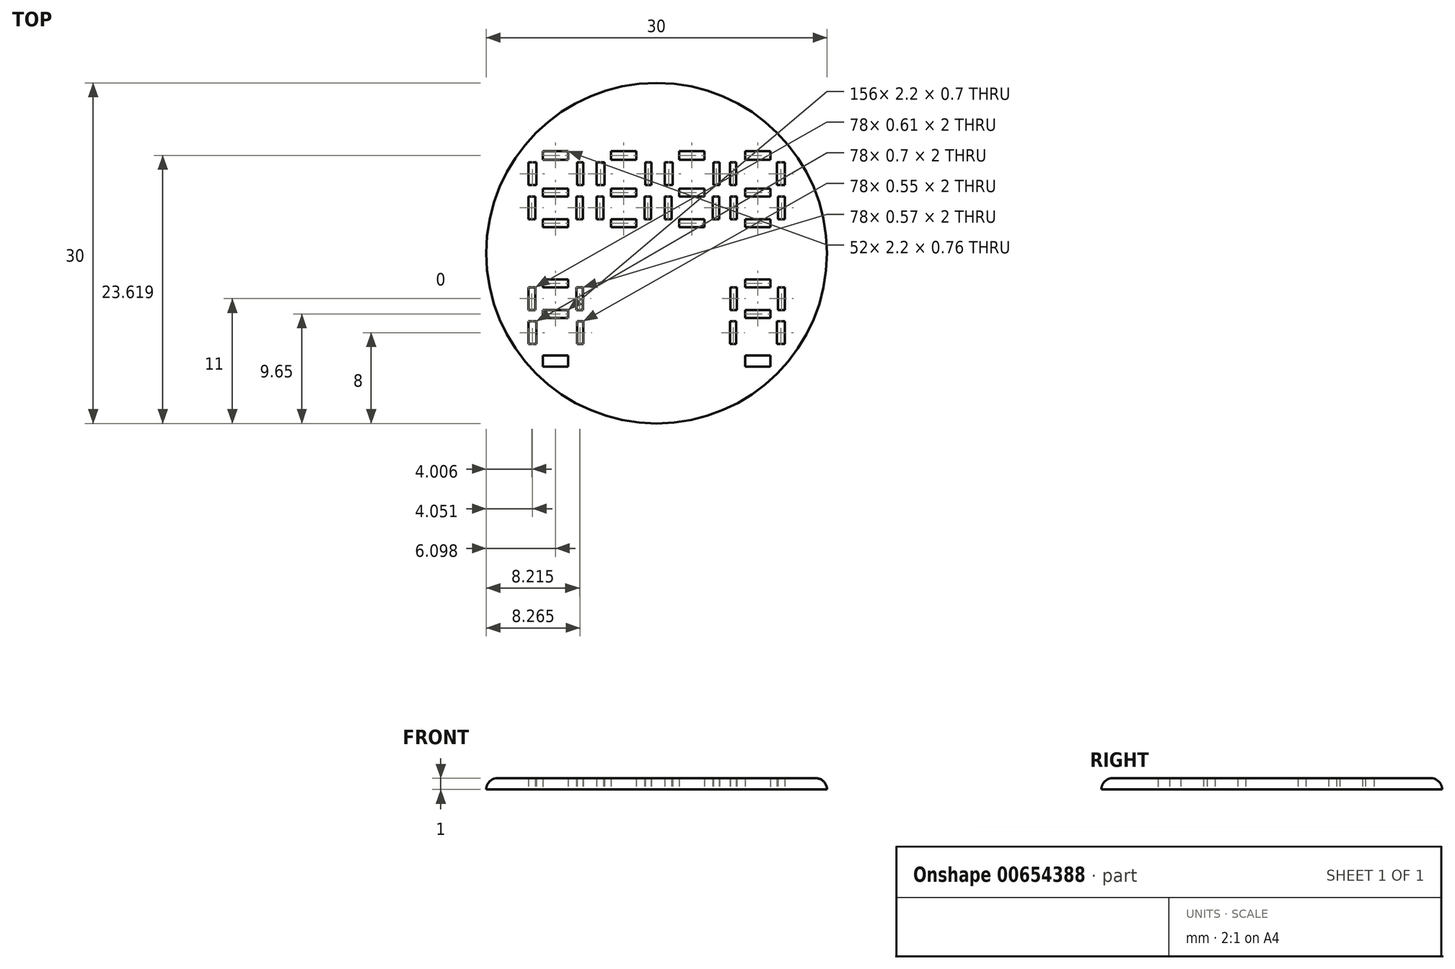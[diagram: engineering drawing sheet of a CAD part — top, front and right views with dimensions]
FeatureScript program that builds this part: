
annotation { "Feature Type Name" : "Feature", "Feature Type Description" : "" }
export const myFeature = defineFeature(function(context is Context, id is Id, definition is map)
    precondition{}
    {
        {
            var Q0;
            Q0=qCreatedBy(makeId("Top.planeOp"),FACE);
            var sketch = newSketch(context, id + "F0", { "sketchPlane" : qUnion([Q0])});
            skCircle(sketch, "E0", {"center": v(0, 0) * mm, "radius": 15 * mm});
            skLineSegment(sketch, "E1.bottom", {"start": v(-6.46, -6) * mm, "end": v(-7, -6) * mm});
            skLineSegment(sketch, "E1.top", {"start": v(-6.46, -8) * mm, "end": v(-7, -8) * mm});
            skLineSegment(sketch, "E1.left", {"start": v(-6.46, -6) * mm, "end": v(-6.46, -8) * mm});
            skLineSegment(sketch, "E1.right", {"start": v(-7, -6) * mm, "end": v(-7, -8) * mm});
            skLineSegment(sketch, "E2.bottom", {"start": v(-7.07, -5) * mm, "end": v(-6.5, -5) * mm});
            skLineSegment(sketch, "E2.top", {"start": v(-7.07, -3) * mm, "end": v(-6.5, -3) * mm});
            skLineSegment(sketch, "E2.left", {"start": v(-7.07, -5) * mm, "end": v(-7.07, -3) * mm});
            skLineSegment(sketch, "E2.right", {"start": v(-6.5, -5) * mm, "end": v(-6.5, -3) * mm});
            skLineSegment(sketch, "E3.bottom", {"start": v(-7.8, -5) * mm, "end": v(-10, -5) * mm});
            skLineSegment(sketch, "E3.top", {"start": v(-7.8, -5.7) * mm, "end": v(-10, -5.7) * mm});
            skLineSegment(sketch, "E3.left", {"start": v(-7.8, -5) * mm, "end": v(-7.8, -5.7) * mm});
            skLineSegment(sketch, "E3.right", {"start": v(-10, -5) * mm, "end": v(-10, -5.7) * mm});
            skLineSegment(sketch, "E4.bottom", {"start": v(-7.8, -9) * mm, "end": v(-10, -9) * mm});
            skLineSegment(sketch, "E4.top", {"start": v(-7.8, -9) * mm, "end": v(-10, -9) * mm});
            skLineSegment(sketch, "E4.left", {"start": v(-7.8, -9) * mm, "end": v(-7.8, -9) * mm});
            skLineSegment(sketch, "E4.right", {"start": v(-10, -9) * mm, "end": v(-10, -9) * mm});
            skLineSegment(sketch, "E5.bottom", {"start": v(-10, -3) * mm, "end": v(-7.8, -3) * mm});
            skLineSegment(sketch, "E5.top", {"start": v(-10, -2.3) * mm, "end": v(-7.8, -2.3) * mm});
            skLineSegment(sketch, "E5.left", {"start": v(-10, -3) * mm, "end": v(-10, -2.3) * mm});
            skLineSegment(sketch, "E5.right", {"start": v(-7.8, -3) * mm, "end": v(-7.8, -2.3) * mm});
            skPoint(sketch, "E6.firstSnap0", {"position": v(-8.9, -3) * mm});
            skLineSegment(sketch, "E6.bottom", {"start": v(-10.69, -3) * mm, "end": v(-11.3, -3) * mm});
            skLineSegment(sketch, "E6.top", {"start": v(-10.69, -5) * mm, "end": v(-11.3, -5) * mm});
            skLineSegment(sketch, "E6.left", {"start": v(-10.69, -3) * mm, "end": v(-10.69, -5) * mm});
            skLineSegment(sketch, "E6.right", {"start": v(-11.3, -3) * mm, "end": v(-11.3, -5) * mm});
            skLineSegment(sketch, "E7.bottom", {"start": v(-10.6, -6) * mm, "end": v(-11.3, -6) * mm});
            skLineSegment(sketch, "E7.top", {"start": v(-10.6, -8) * mm, "end": v(-11.3, -8) * mm});
            skLineSegment(sketch, "E7.left", {"start": v(-10.6, -6) * mm, "end": v(-10.6, -8) * mm});
            skLineSegment(sketch, "E7.right", {"start": v(-11.3, -6) * mm, "end": v(-11.3, -8) * mm});
            skLineSegment(sketch, "E8.MirrorCS", {"start": v(10.69, -3) * mm, "end": v(10.69, -5) * mm});
            skLineSegment(sketch, "E9.MirrorCS", {"start": v(10.69, -5) * mm, "end": v(11.3, -5) * mm});
            skLineSegment(sketch, "E10.MirrorCS", {"start": v(11.3, -3) * mm, "end": v(11.3, -5) * mm});
            skLineSegment(sketch, "E11.MirrorCS", {"start": v(10.69, -3) * mm, "end": v(11.3, -3) * mm});
            skLineSegment(sketch, "E12.MirrorCS", {"start": v(7.8, -5.7) * mm, "end": v(10, -5.7) * mm});
            skLineSegment(sketch, "E13.MirrorCS", {"start": v(7.8, -5) * mm, "end": v(10, -5) * mm});
            skLineSegment(sketch, "E14.MirrorCS", {"start": v(7.8, -5) * mm, "end": v(7.8, -5.7) * mm});
            skLineSegment(sketch, "E15.MirrorCS", {"start": v(7.07, -5) * mm, "end": v(6.5, -5) * mm});
            skLineSegment(sketch, "E16.MirrorCS", {"start": v(6.5, -5) * mm, "end": v(6.5, -3) * mm});
            skLineSegment(sketch, "E17.MirrorCS", {"start": v(7.07, -3) * mm, "end": v(6.5, -3) * mm});
            skLineSegment(sketch, "E18.MirrorCS", {"start": v(7.07, -5) * mm, "end": v(7.07, -3) * mm});
            skLineSegment(sketch, "E19.MirrorCS", {"start": v(6.46, -6) * mm, "end": v(7, -6) * mm});
            skLineSegment(sketch, "E20.MirrorCS", {"start": v(6.46, -6) * mm, "end": v(6.46, -8) * mm});
            skLineSegment(sketch, "E21.MirrorCS", {"start": v(6.46, -8) * mm, "end": v(7, -8) * mm});
            skLineSegment(sketch, "E22.MirrorCS", {"start": v(7, -6) * mm, "end": v(7, -8) * mm});
            skLineSegment(sketch, "E23.MirrorCS", {"start": v(7.8, -9) * mm, "end": v(10, -9) * mm});
            skLineSegment(sketch, "E24.MirrorCS", {"start": v(7.8, -9) * mm, "end": v(7.8, -9) * mm});
            skLineSegment(sketch, "E25.MirrorCS", {"start": v(10, -9) * mm, "end": v(10, -9) * mm});
            skLineSegment(sketch, "E26.MirrorCS", {"start": v(10.6, -6) * mm, "end": v(10.6, -8) * mm});
            skLineSegment(sketch, "E27.MirrorCS", {"start": v(11.3, -6) * mm, "end": v(11.3, -8) * mm});
            skLineSegment(sketch, "E28.MirrorCS", {"start": v(10.6, -8) * mm, "end": v(11.3, -8) * mm});
            skLineSegment(sketch, "E29.MirrorCS", {"start": v(10.6, -6) * mm, "end": v(11.3, -6) * mm});
            skLineSegment(sketch, "E30.MirrorCS", {"start": v(10, -3) * mm, "end": v(7.8, -3) * mm});
            skLineSegment(sketch, "E31.MirrorCS", {"start": v(10, -2.3) * mm, "end": v(7.8, -2.3) * mm});
            skLineSegment(sketch, "E32.MirrorCS", {"start": v(10, -3) * mm, "end": v(10, -2.3) * mm});
            skLineSegment(sketch, "E33.MirrorCS", {"start": v(7.8, -3) * mm, "end": v(7.8, -2.3) * mm});
            skLineSegment(sketch, "E34", {"start": v(10, -5) * mm, "end": v(10, -5.7) * mm});
            skLineSegment(sketch, "E35.MirrorCS", {"start": v(-7.8, 5) * mm, "end": v(-10, 5) * mm});
            skLineSegment(sketch, "E36.MirrorCS", {"start": v(-7.8, 5.7) * mm, "end": v(-10, 5.7) * mm});
            skLineSegment(sketch, "E37.MirrorCS", {"start": v(-7.8, 5) * mm, "end": v(-7.8, 5.7) * mm});
            skLineSegment(sketch, "E38.MirrorCS", {"start": v(-10, 5) * mm, "end": v(-10, 5.7) * mm});
            skLineSegment(sketch, "E39.MirrorCS", {"start": v(-7, 6) * mm, "end": v(-7, 8) * mm});
            skLineSegment(sketch, "E40.MirrorCS", {"start": v(-6.46, 6) * mm, "end": v(-7, 6) * mm});
            skLineSegment(sketch, "E41.MirrorCS", {"start": v(-6.46, 6) * mm, "end": v(-6.46, 8) * mm});
            skLineSegment(sketch, "E42.MirrorCS", {"start": v(-6.46, 8) * mm, "end": v(-7, 8) * mm});
            skLineSegment(sketch, "E43.MirrorCS", {"start": v(-6.5, 5) * mm, "end": v(-6.5, 3) * mm});
            skLineSegment(sketch, "E44.MirrorCS", {"start": v(-7.07, 5) * mm, "end": v(-6.5, 5) * mm});
            skLineSegment(sketch, "E45.MirrorCS", {"start": v(-7.07, 5) * mm, "end": v(-7.07, 3) * mm});
            skLineSegment(sketch, "E46.MirrorCS", {"start": v(-7.07, 3) * mm, "end": v(-6.5, 3) * mm});
            skLineSegment(sketch, "E47.MirrorCS", {"start": v(-10, 3) * mm, "end": v(-7.8, 3) * mm});
            skLineSegment(sketch, "E48.MirrorCS", {"start": v(-10, 2.3) * mm, "end": v(-7.8, 2.3) * mm});
            skLineSegment(sketch, "E49.MirrorCS", {"start": v(-7.8, 3) * mm, "end": v(-7.8, 2.3) * mm});
            skLineSegment(sketch, "E50.MirrorCS", {"start": v(-10, 3) * mm, "end": v(-10, 2.3) * mm});
            skLineSegment(sketch, "E51.MirrorCS", {"start": v(-10.69, 3) * mm, "end": v(-10.69, 5) * mm});
            skLineSegment(sketch, "E52.MirrorCS", {"start": v(-10.69, 3) * mm, "end": v(-11.3, 3) * mm});
            skLineSegment(sketch, "E53.MirrorCS", {"start": v(-11.3, 3) * mm, "end": v(-11.3, 5) * mm});
            skLineSegment(sketch, "E54.MirrorCS", {"start": v(-10.69, 5) * mm, "end": v(-11.3, 5) * mm});
            skLineSegment(sketch, "E55.MirrorCS", {"start": v(-10.6, 6) * mm, "end": v(-10.6, 8) * mm});
            skLineSegment(sketch, "E56.MirrorCS", {"start": v(-11.3, 6) * mm, "end": v(-11.3, 8) * mm});
            skLineSegment(sketch, "E57.MirrorCS", {"start": v(-10.6, 8) * mm, "end": v(-11.3, 8) * mm});
            skLineSegment(sketch, "E58.MirrorCS", {"start": v(-10.6, 6) * mm, "end": v(-11.3, 6) * mm});
            skLineSegment(sketch, "E59.MirrorCS", {"start": v(-7.8, 9) * mm, "end": v(-10, 9) * mm});
            skLineSegment(sketch, "E60.MirrorCS", {"start": v(-7.8, 9) * mm, "end": v(-7.8, 9) * mm});
            skLineSegment(sketch, "E61.MirrorCS", {"start": v(-10, 9) * mm, "end": v(-10, 9) * mm});
            skLineSegment(sketch, "E62", {"start": v(-10, 9) * mm, "end": v(-10, 8.24) * mm});
            skLineSegment(sketch, "E63", {"start": v(-10, 8.24) * mm, "end": v(-7.8, 8.24) * mm});
            skLineSegment(sketch, "E64", {"start": v(-7.8, 8.24) * mm, "end": v(-7.8, 9) * mm});
            skLineSegment(sketch, "E65", {"start": v(-7.8, -9) * mm, "end": v(-7.8, -10) * mm});
            skLineSegment(sketch, "E66", {"start": v(-10, -9) * mm, "end": v(-10, -10) * mm});
            skLineSegment(sketch, "E67", {"start": v(-10, -10) * mm, "end": v(-7.8, -10) * mm});
            skLineSegment(sketch, "E68", {"start": v(7.8, -9) * mm, "end": v(7.8, -10) * mm});
            skLineSegment(sketch, "E69", {"start": v(7.8, -10) * mm, "end": v(10, -10) * mm});
            skLineSegment(sketch, "E70", {"start": v(10, -10) * mm, "end": v(10, -9) * mm});
            skLineSegment(sketch, "E71.MirrorCS", {"start": v(10, 2.3) * mm, "end": v(7.8, 2.3) * mm});
            skLineSegment(sketch, "E72.MirrorCS", {"start": v(10, 3) * mm, "end": v(7.8, 3) * mm});
            skLineSegment(sketch, "E73.MirrorCS", {"start": v(6.5, 5) * mm, "end": v(6.5, 3) * mm});
            skLineSegment(sketch, "E74.MirrorCS", {"start": v(7.07, 5) * mm, "end": v(7.07, 3) * mm});
            skLineSegment(sketch, "E75.MirrorCS", {"start": v(7.8, 3) * mm, "end": v(7.8, 2.3) * mm});
            skLineSegment(sketch, "E76.MirrorCS", {"start": v(10, 3) * mm, "end": v(10, 2.3) * mm});
            skLineSegment(sketch, "E77.MirrorCS", {"start": v(7.07, 3) * mm, "end": v(6.5, 3) * mm});
            skLineSegment(sketch, "E78.MirrorCS", {"start": v(7.07, 5) * mm, "end": v(6.5, 5) * mm});
            skLineSegment(sketch, "E79.MirrorCS", {"start": v(10.69, 3) * mm, "end": v(11.3, 3) * mm});
            skLineSegment(sketch, "E80.MirrorCS", {"start": v(10.69, 5) * mm, "end": v(11.3, 5) * mm});
            skLineSegment(sketch, "E81.MirrorCS", {"start": v(10.69, 3) * mm, "end": v(10.69, 5) * mm});
            skLineSegment(sketch, "E82.MirrorCS", {"start": v(11.3, 3) * mm, "end": v(11.3, 5) * mm});
            skLineSegment(sketch, "E83.MirrorCS", {"start": v(7.8, 5) * mm, "end": v(10, 5) * mm});
            skLineSegment(sketch, "E84.MirrorCS", {"start": v(7.8, 5) * mm, "end": v(7.8, 5.7) * mm});
            skLineSegment(sketch, "E85.MirrorCS", {"start": v(10, 5) * mm, "end": v(10, 5.7) * mm});
            skLineSegment(sketch, "E86.MirrorCS", {"start": v(7.8, 5.7) * mm, "end": v(10, 5.7) * mm});
            skLineSegment(sketch, "E87.MirrorCS", {"start": v(6.46, 6) * mm, "end": v(7, 6) * mm});
            skLineSegment(sketch, "E88.MirrorCS", {"start": v(7, 6) * mm, "end": v(7, 8) * mm});
            skLineSegment(sketch, "E89.MirrorCS", {"start": v(6.46, 6) * mm, "end": v(6.46, 8) * mm});
            skLineSegment(sketch, "E90.MirrorCS", {"start": v(6.46, 8) * mm, "end": v(7, 8) * mm});
            skLineSegment(sketch, "E91.MirrorCS", {"start": v(10.6, 6) * mm, "end": v(10.6, 8) * mm});
            skLineSegment(sketch, "E92.MirrorCS", {"start": v(10.6, 6) * mm, "end": v(11.3, 6) * mm});
            skLineSegment(sketch, "E93.MirrorCS", {"start": v(11.3, 6) * mm, "end": v(11.3, 8) * mm});
            skLineSegment(sketch, "E94.MirrorCS", {"start": v(10.6, 8) * mm, "end": v(11.3, 8) * mm});
            skLineSegment(sketch, "E95.MirrorCS", {"start": v(10, 8.24) * mm, "end": v(7.8, 8.24) * mm});
            skLineSegment(sketch, "E96.MirrorCS", {"start": v(7.8, 9) * mm, "end": v(10, 9) * mm});
            skLineSegment(sketch, "E97.MirrorCS", {"start": v(7.8, 8.24) * mm, "end": v(7.8, 9) * mm});
            skLineSegment(sketch, "E98.MirrorCS", {"start": v(10, 9) * mm, "end": v(10, 8.24) * mm});
            skLineSegment(sketch, "E99.1.0.0", {"start": v(-5.3, 6) * mm, "end": v(-5.3, 8) * mm});
            skLineSegment(sketch, "E99.1.0.1", {"start": v(-4, 3) * mm, "end": v(-1.8, 3) * mm});
            skLineSegment(sketch, "E99.1.0.2", {"start": v(-1.07, 5) * mm, "end": v(-1.07, 3) * mm});
            skLineSegment(sketch, "E99.1.0.3", {"start": v(-4.6, 6) * mm, "end": v(-4.6, 8) * mm});
            skLineSegment(sketch, "E99.1.0.4", {"start": v(-4, 8.24) * mm, "end": v(-1.8, 8.24) * mm});
            skLineSegment(sketch, "E99.1.0.5", {"start": v(-1, 6) * mm, "end": v(-1, 8) * mm});
            skLineSegment(sketch, "E99.1.0.6", {"start": v(-1.8, 5.7) * mm, "end": v(-4, 5.7) * mm});
            skLineSegment(sketch, "E99.1.0.7", {"start": v(-1.8, 9) * mm, "end": v(-4, 9) * mm});
            skLineSegment(sketch, "E99.1.0.8", {"start": v(-4, 2.3) * mm, "end": v(-1.8, 2.3) * mm});
            skLineSegment(sketch, "E99.1.0.9", {"start": v(-4.69, 3) * mm, "end": v(-4.69, 5) * mm});
            skLineSegment(sketch, "E99.1.0.10", {"start": v(-0.46, 6) * mm, "end": v(-0.46, 8) * mm});
            skLineSegment(sketch, "E99.1.0.11", {"start": v(-0.5, 5) * mm, "end": v(-0.5, 3) * mm});
            skLineSegment(sketch, "E99.1.0.12", {"start": v(-5.3, 3) * mm, "end": v(-5.3, 5) * mm});
            skLineSegment(sketch, "E99.1.0.13", {"start": v(-1.8, 8.24) * mm, "end": v(-1.8, 9) * mm});
            skLineSegment(sketch, "E99.1.0.14", {"start": v(-4, 9) * mm, "end": v(-4, 8.24) * mm});
            skLineSegment(sketch, "E99.1.0.15", {"start": v(-1.8, 5) * mm, "end": v(-4, 5) * mm});
            skLineSegment(sketch, "E99.1.0.16", {"start": v(-1.8, 3) * mm, "end": v(-1.8, 2.3) * mm});
            skLineSegment(sketch, "E99.1.0.17", {"start": v(-4.69, 5) * mm, "end": v(-5.3, 5) * mm});
            skLineSegment(sketch, "E99.1.0.18", {"start": v(-4.6, 6) * mm, "end": v(-5.3, 6) * mm});
            skLineSegment(sketch, "E99.1.0.19", {"start": v(-0.46, 8) * mm, "end": v(-1, 8) * mm});
            skLineSegment(sketch, "E99.1.0.20", {"start": v(-4.69, 3) * mm, "end": v(-5.3, 3) * mm});
            skLineSegment(sketch, "E99.1.0.21", {"start": v(-4.6, 8) * mm, "end": v(-5.3, 8) * mm});
            skLineSegment(sketch, "E99.1.0.22", {"start": v(-1.8, 5) * mm, "end": v(-1.8, 5.7) * mm});
            skLineSegment(sketch, "E99.1.0.23", {"start": v(-1.07, 3) * mm, "end": v(-0.5, 3) * mm});
            skLineSegment(sketch, "E99.1.0.24", {"start": v(-1.07, 5) * mm, "end": v(-0.5, 5) * mm});
            skLineSegment(sketch, "E99.1.0.25", {"start": v(-4, 5) * mm, "end": v(-4, 5.7) * mm});
            skLineSegment(sketch, "E99.1.0.26", {"start": v(-4, 3) * mm, "end": v(-4, 2.3) * mm});
            skLineSegment(sketch, "E99.1.0.27", {"start": v(-0.46, 6) * mm, "end": v(-1, 6) * mm});
            skLineSegment(sketch, "E99.1.0.28", {"start": v(-0.46, 6) * mm, "end": v(-1, 6) * mm});
            skLineSegment(sketch, "E99.2.0.0", {"start": v(0.7, 6) * mm, "end": v(0.7, 8) * mm});
            skLineSegment(sketch, "E99.2.0.1", {"start": v(2, 3) * mm, "end": v(4.2, 3) * mm});
            skLineSegment(sketch, "E99.2.0.2", {"start": v(4.93, 5) * mm, "end": v(4.93, 3) * mm});
            skLineSegment(sketch, "E99.2.0.3", {"start": v(1.4, 6) * mm, "end": v(1.4, 8) * mm});
            skLineSegment(sketch, "E99.2.0.4", {"start": v(2, 8.24) * mm, "end": v(4.2, 8.24) * mm});
            skLineSegment(sketch, "E99.2.0.5", {"start": v(5, 6) * mm, "end": v(5, 8) * mm});
            skLineSegment(sketch, "E99.2.0.6", {"start": v(4.2, 5.7) * mm, "end": v(2, 5.7) * mm});
            skLineSegment(sketch, "E99.2.0.7", {"start": v(4.2, 9) * mm, "end": v(2, 9) * mm});
            skLineSegment(sketch, "E99.2.0.8", {"start": v(2, 2.3) * mm, "end": v(4.2, 2.3) * mm});
            skLineSegment(sketch, "E99.2.0.9", {"start": v(1.31, 3) * mm, "end": v(1.31, 5) * mm});
            skLineSegment(sketch, "E99.2.0.10", {"start": v(5.54, 6) * mm, "end": v(5.54, 8) * mm});
            skLineSegment(sketch, "E99.2.0.11", {"start": v(5.5, 5) * mm, "end": v(5.5, 3) * mm});
            skLineSegment(sketch, "E99.2.0.12", {"start": v(0.7, 3) * mm, "end": v(0.7, 5) * mm});
            skLineSegment(sketch, "E99.2.0.13", {"start": v(4.2, 8.24) * mm, "end": v(4.2, 9) * mm});
            skLineSegment(sketch, "E99.2.0.14", {"start": v(2, 9) * mm, "end": v(2, 8.24) * mm});
            skLineSegment(sketch, "E99.2.0.15", {"start": v(4.2, 5) * mm, "end": v(2, 5) * mm});
            skLineSegment(sketch, "E99.2.0.16", {"start": v(4.2, 3) * mm, "end": v(4.2, 2.3) * mm});
            skLineSegment(sketch, "E99.2.0.17", {"start": v(1.31, 5) * mm, "end": v(0.7, 5) * mm});
            skLineSegment(sketch, "E99.2.0.18", {"start": v(1.4, 6) * mm, "end": v(0.7, 6) * mm});
            skLineSegment(sketch, "E99.2.0.19", {"start": v(5.54, 8) * mm, "end": v(5, 8) * mm});
            skLineSegment(sketch, "E99.2.0.20", {"start": v(1.31, 3) * mm, "end": v(0.7, 3) * mm});
            skLineSegment(sketch, "E99.2.0.21", {"start": v(1.4, 8) * mm, "end": v(0.7, 8) * mm});
            skLineSegment(sketch, "E99.2.0.22", {"start": v(4.2, 5) * mm, "end": v(4.2, 5.7) * mm});
            skLineSegment(sketch, "E99.2.0.23", {"start": v(4.93, 3) * mm, "end": v(5.5, 3) * mm});
            skLineSegment(sketch, "E99.2.0.24", {"start": v(4.93, 5) * mm, "end": v(5.5, 5) * mm});
            skLineSegment(sketch, "E99.2.0.25", {"start": v(2, 5) * mm, "end": v(2, 5.7) * mm});
            skLineSegment(sketch, "E99.2.0.26", {"start": v(2, 3) * mm, "end": v(2, 2.3) * mm});
            skLineSegment(sketch, "E99.2.0.27", {"start": v(5.54, 6) * mm, "end": v(5, 6) * mm});
            skLineSegment(sketch, "E99.2.0.28", {"start": v(5.54, 6) * mm, "end": v(5, 6) * mm});
            skLineSegment(sketch, "E99.direction1", {"start": v(-11.3, 3) * mm, "end": v(-5.3, 3) * mm, "construction": true});
            skSolve(sketch);
        }
        {
            var Q0;
            Q0=makeQuery(id+"F0.imprint","IMPRINT",FACE,{"disambiguationData":[TD([[makeQuery(id+"F0.imprint","IMPRINT",EDGE,{"derivedFrom":sQuery(id+"F0.wireOp",EDGE,"E0")}),1.0]])]});
            var Q1;
            Q1=makeQuery(id+"F0.imprint","IMPRINT",FACE,{"disambiguationData":[TD([[makeQuery(id+"F0.imprint","IMPRINT",EDGE,{"derivedFrom":sQuery(id+"F0.wireOp",EDGE,"bd14f3e4-5af1-4a7d-9640-db2f7e966477.sketch_text.stroke-23")}),1.0]])]});
            var Q2;
            Q2=makeQuery(id+"F0.imprint","IMPRINT",FACE,{"disambiguationData":[TD([[makeQuery(id+"F0.imprint","IMPRINT",EDGE,{"derivedFrom":sQuery(id+"F0.wireOp",EDGE,"bd14f3e4-5af1-4a7d-9640-db2f7e966477.sketch_text.stroke-16")}),1.0]])]});
            var Q3;
            Q3=makeQuery(id+"F0.imprint","IMPRINT",FACE,{"disambiguationData":[TD([[makeQuery(id+"F0.imprint","IMPRINT",EDGE,{"derivedFrom":sQuery(id+"F0.wireOp",EDGE,"bd14f3e4-5af1-4a7d-9640-db2f7e966477.sketch_text.stroke-47")}),1.0]])]});
            var Q4;
            Q4=makeQuery(id+"F0.imprint","IMPRINT",FACE,{"disambiguationData":[TD([[makeQuery(id+"F0.imprint","IMPRINT",EDGE,{"derivedFrom":sQuery(id+"F0.wireOp",EDGE,"bd14f3e4-5af1-4a7d-9640-db2f7e966477.sketch_text.stroke-54")}),1.0]])]});
            var Q5;
            Q5=makeQuery(id+"F0.imprint","IMPRINT",FACE,{"disambiguationData":[TD([[makeQuery(id+"F0.imprint","IMPRINT",EDGE,{"derivedFrom":sQuery(id+"F0.wireOp",EDGE,"bd14f3e4-5af1-4a7d-9640-db2f7e966477.sketch_text.stroke-101")}),1.0]])]});
            var Q6;
            Q6=makeQuery(id+"F0.imprint","IMPRINT",FACE,{"disambiguationData":[TD([[makeQuery(id+"F0.imprint","IMPRINT",EDGE,{"derivedFrom":sQuery(id+"F0.wireOp",EDGE,"bd14f3e4-5af1-4a7d-9640-db2f7e966477.sketch_text.stroke-94")}),1.0]])]});
            var Q7;
            Q7=makeQuery(id+"F0.imprint","IMPRINT",FACE,{"disambiguationData":[TD([[makeQuery(id+"F0.imprint","IMPRINT",EDGE,{"derivedFrom":sQuery(id+"F0.wireOp",EDGE,"bd14f3e4-5af1-4a7d-9640-db2f7e966477.sketch_text.stroke-125")}),1.0]])]});
            var Q8;
            Q8=makeQuery(id+"F0.imprint","IMPRINT",FACE,{"disambiguationData":[TD([[makeQuery(id+"F0.imprint","IMPRINT",EDGE,{"derivedFrom":sQuery(id+"F0.wireOp",EDGE,"bd14f3e4-5af1-4a7d-9640-db2f7e966477.sketch_text.stroke-132")}),1.0]])]});
            var Q9;
            Q9=makeQuery(id+"F0.imprint","IMPRINT",FACE,{"disambiguationData":[TD([[makeQuery(id+"F0.imprint","IMPRINT",EDGE,{"derivedFrom":sQuery(id+"F0.wireOp",EDGE,"1741a0bf-e769-4358-ab37-6a426c443f57.sketch_text.stroke-23")}),1.0]])]});
            var Q10;
            Q10=makeQuery(id+"F0.imprint","IMPRINT",FACE,{"disambiguationData":[TD([[makeQuery(id+"F0.imprint","IMPRINT",EDGE,{"derivedFrom":sQuery(id+"F0.wireOp",EDGE,"1741a0bf-e769-4358-ab37-6a426c443f57.sketch_text.stroke-15")}),1.0]])]});
            var Q11;
            Q11=makeQuery(id+"F0.imprint","IMPRINT",FACE,{"disambiguationData":[TD([[makeQuery(id+"F0.imprint","IMPRINT",EDGE,{"derivedFrom":sQuery(id+"F0.wireOp",EDGE,"1741a0bf-e769-4358-ab37-6a426c443f57.sketch_text.stroke-62")}),1.0]])]});
            var Q12;
            Q12=makeQuery(id+"F0.imprint","IMPRINT",FACE,{"disambiguationData":[TD([[makeQuery(id+"F0.imprint","IMPRINT",EDGE,{"derivedFrom":sQuery(id+"F0.wireOp",EDGE,"1741a0bf-e769-4358-ab37-6a426c443f57.sketch_text.stroke-54")}),1.0]])]});
            extrude(context, id + "F1", {"entities" : qUnion([Q0, Q1, Q2, Q3, Q4, Q5, Q6, Q7, Q8, Q9, Q10, Q11, Q12]), "depth" : 1 * mm, "offsetDistance" : 25 * mm});
        }
        {
            var Q0;
            Q0=makeQuery(id+"F1.opExtrude","CAP_EDGE",EDGE,{"disambiguationData":[OSD([sQuery(id+"F0.wireOp",EDGE,"E0")])],"isStart":false});
            fillet(context, id + "F2", {"entities" : qUnion([Q0]), "radius" : 1 * mm, "tangentPropagation" : true, "allowEdgeOverflow" : false});
        }
    });
